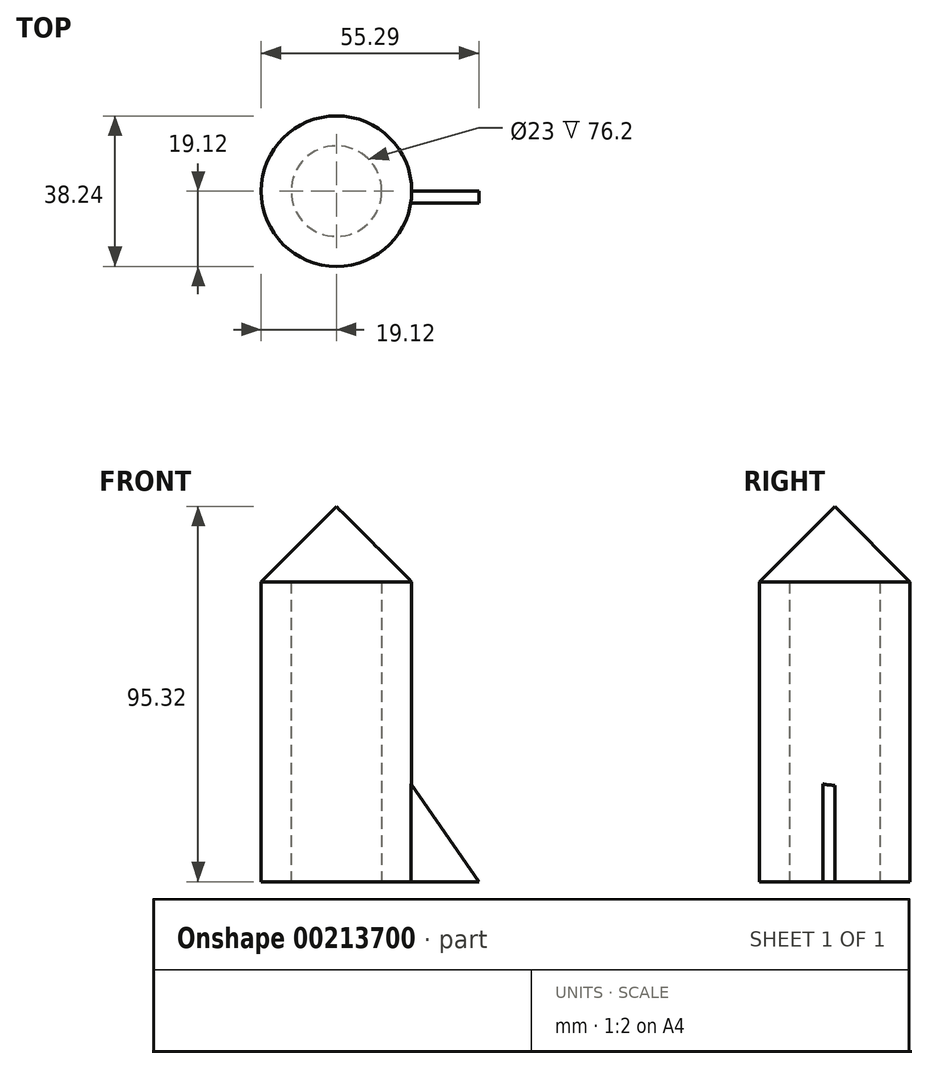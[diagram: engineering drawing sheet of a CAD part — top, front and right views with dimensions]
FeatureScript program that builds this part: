
annotation { "Feature Type Name" : "Feature", "Feature Type Description" : "" }
export const myFeature = defineFeature(function(context is Context, id is Id, definition is map)
    precondition{}
    {
        {
            var Q0;
            Q0=qCreatedBy(makeId("Top.planeOp"),FACE);
            var sketch = newSketch(context, id + "F0", { "sketchPlane" : qUnion([Q0])});
            skCircle(sketch, "E0", {"center": v(0, 0) * mm, "radius": 11.5 * mm});
            skCircle(sketch, "E1", {"center": v(0, 0) * mm, "radius": 19.12 * mm});
            skSolve(sketch);
        }
        {
            var Q0;
            Q0=makeQuery(id+"F0.imprint","IMPRINT",FACE,{"disambiguationData":[TD([[makeQuery(id+"F0.imprint","IMPRINT",EDGE,{"derivedFrom":sQuery(id+"F0.wireOp",EDGE,"E0")}),-1.0]])]});
            extrude(context, id + "F1", {"entities" : qUnion([Q0]), "depth" : 76.2 * mm});
        }
        {
            var Q0;
            Q0=makeQuery(id+"F1.opExtrude","CAP_FACE",FACE,{"disambiguationData":[OSD([sQuery(id+"F0.wireOp",EDGE,"E0"),sQuery(id+"F0.wireOp",EDGE,"E1")])],"isStart":false});
            var sketch = newSketch(context, id + "F2", { "sketchPlane" : qUnion([Q0])});
            skCircle(sketch, "E2.0", {"center": v(0, 0) * mm, "radius": 19.12 * mm});
            skSolve(sketch);
        }
        {
            var Q0;
            Q0 = qSketchRegion(id + "F2", true);
            extrude(context, id + "F3", {"entities" : qUnion([Q0]), "operationType" : NewBodyOperationType.ADD, "depth" : 27.94 * mm, "hasDraft" : true, "draftAngle" : 45 * degree, "draftPullDirection" : true});
        }
        {
            var Q0;
            Q0=qCreatedBy(makeId("Front.planeOp"),FACE);
            var sketch = newSketch(context, id + "F4", { "sketchPlane" : qUnion([Q0])});
            skLineSegment(sketch, "E3", {"start": v(17.35, 27.03) * mm, "end": v(36.17, 0) * mm});
            skLineSegment(sketch, "E4", {"start": v(36.17, 0) * mm, "end": v(16.62, 0) * mm});
            skLineSegment(sketch, "E5", {"start": v(16.62, 0) * mm, "end": v(17.35, 27.03) * mm});
            skSolve(sketch);
        }
        {
            var Q0;
            Q0=makeQuery(id+"F4.imprint","IMPRINT",FACE,{"disambiguationData":[TD([[makeQuery(id+"F4.imprint","IMPRINT",EDGE,{"derivedFrom":sQuery(id+"F4.wireOp",EDGE,"E3")}),-1.0]])]});
            extrude(context, id + "F5", {"entities" : qUnion([Q0]), "operationType" : NewBodyOperationType.ADD, "depth" : 3 * mm});
        }
    });
